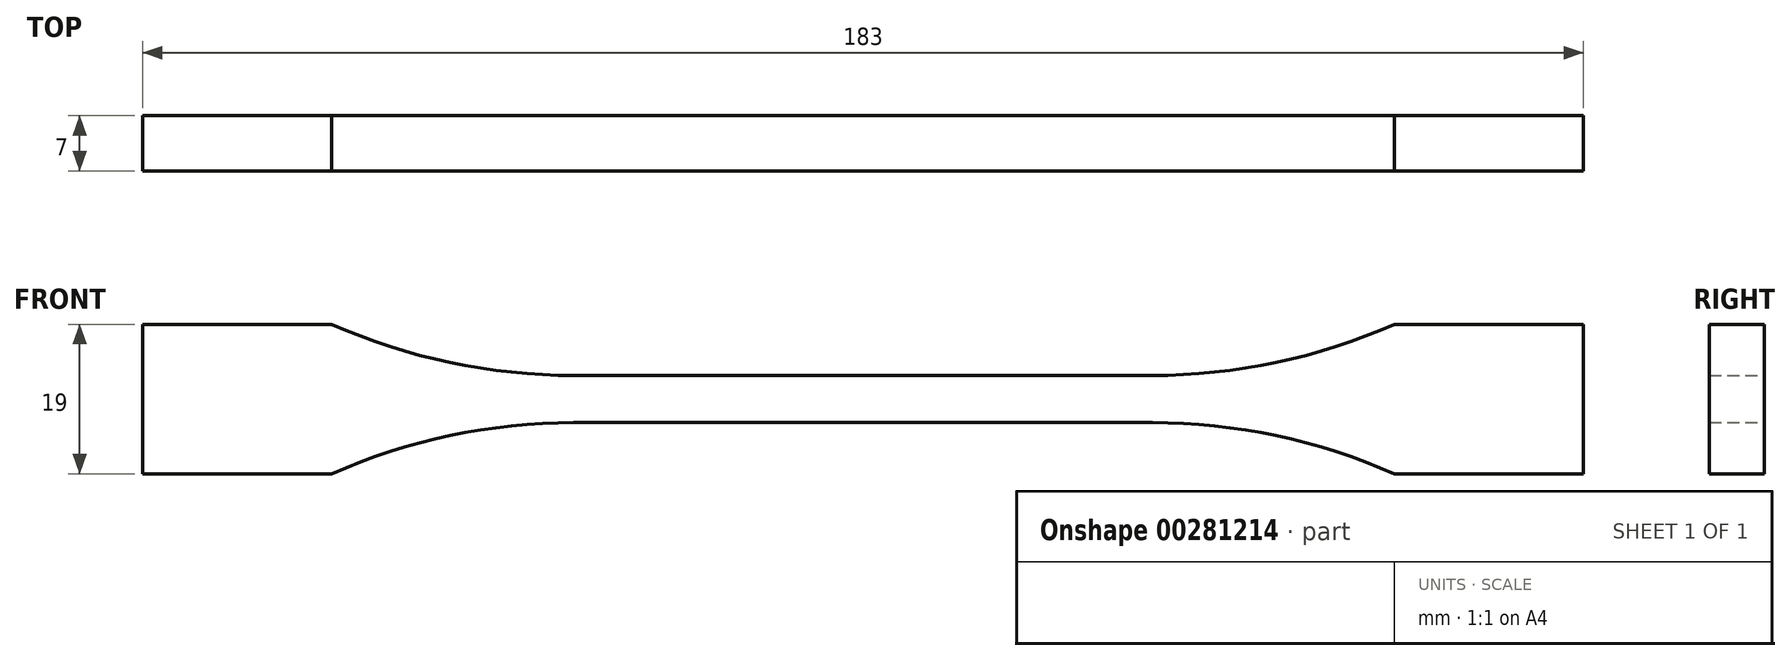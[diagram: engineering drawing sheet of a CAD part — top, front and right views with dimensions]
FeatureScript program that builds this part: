
annotation { "Feature Type Name" : "Feature", "Feature Type Description" : "" }
export const myFeature = defineFeature(function(context is Context, id is Id, definition is map)
    precondition{}
    {
        {
            var Q0;
            Q0=qCreatedBy(makeId("Front.planeOp"),FACE);
            var sketch = newSketch(context, id + "F0", { "sketchPlane" : qUnion([Q0])});
            skLineSegment(sketch, "E0", {"start": v(0, 3) * mm, "end": v(36.75, 3) * mm});
            skArc(sketch, "E1", {"start": v(36.75, 3) * mm, "mid": v(52.46, 4.64) * mm, "end": v(67.5, 9.5) * mm});
            skLineSegment(sketch, "E2", {"start": v(67.5, 9.5) * mm, "end": v(91.5, 9.5) * mm});
            skLineSegment(sketch, "E3", {"start": v(91.5, 9.5) * mm, "end": v(91.5, 0) * mm});
            skLineSegment(sketch, "E4.MirrorCS", {"start": v(0, -3) * mm, "end": v(36.75, -3) * mm});
            skLineSegment(sketch, "E5.MirrorCS", {"start": v(91.5, -9.5) * mm, "end": v(91.5, 0) * mm});
            skLineSegment(sketch, "E6.MirrorCS", {"start": v(67.5, -9.5) * mm, "end": v(91.5, -9.5) * mm});
            skArc(sketch, "E7.MirrorCS", {"start": v(36.75, -3) * mm, "mid": v(52.46, -4.64) * mm, "end": v(67.5, -9.5) * mm});
            skArc(sketch, "E8.MirrorCS", {"start": v(-36.75, -3) * mm, "mid": v(-52.46, -4.64) * mm, "end": v(-67.5, -9.5) * mm});
            skLineSegment(sketch, "E9.MirrorCS", {"start": v(-67.5, -9.5) * mm, "end": v(-91.5, -9.5) * mm});
            skLineSegment(sketch, "E10.MirrorCS", {"start": v(0, 3) * mm, "end": v(-36.75, 3) * mm});
            skArc(sketch, "E11.MirrorCS", {"start": v(-36.75, 3) * mm, "mid": v(-52.46, 4.64) * mm, "end": v(-67.5, 9.5) * mm});
            skLineSegment(sketch, "E12.MirrorCS", {"start": v(-67.5, 9.5) * mm, "end": v(-91.5, 9.5) * mm});
            skLineSegment(sketch, "E13.MirrorCS", {"start": v(-91.5, -9.5) * mm, "end": v(-91.5, 0) * mm});
            skLineSegment(sketch, "E14.MirrorCS", {"start": v(-91.5, 9.5) * mm, "end": v(-91.5, 0) * mm});
            skLineSegment(sketch, "E15.MirrorCS", {"start": v(0, -3) * mm, "end": v(-36.75, -3) * mm});
            skSolve(sketch);
        }
        {
            var Q0;
            Q0 = qSketchRegion(id + "F0", true);
            extrude(context, id + "F1", {"entities" : qUnion([Q0]), "endBound" : BoundingType.SYMMETRIC, "depth" : 7 * mm});
        }
    });
